# Revit family: FF30_Edge.rfa
name_source: partatom
category: 门
units: mm (PartAtom-declared; Revit-internal decimal feet)

## family parameters
主体 = 墙
共享 = 否
加载时剪切的空心 = 否
总是垂直 = 是
房间计算点 = 否

## types (16) — shared parameters
Height above ground = 4' - 0"
Height of Door = 14' - 0"
Width of Switch = 1' - 0"
depth of Switch = 0' - 5"
height of Switch = 1' - 4"
高度 = 14' - 0"
默认高程 = 0' - 0"

## per-type parameters (varying)
| type | LAYOUT K | LAYOUT L | LAYOUT M | LAYOUT N | LAYOUT P | LAYOUT Q | LAYOUT R | LAYOUT S | Width | Width of Door | 宽度 |
| LAYOUT K 14'x14' | 是 | 否 | 否 | 否 | 否 | 否 | 否 | 否 | 14' - 0" | 14' - 0" | 14' - 0" |
| LAYOUT L 14'x14' | 否 | 是 | 否 | 否 | 否 | 否 | 否 | 否 | 14' - 0" | 14' - 0" | 14' - 0" |
| LAYOUT M 14'x14' | 否 | 否 | 是 | 否 | 否 | 否 | 否 | 否 | 14' - 0" | 14' - 0" | 14' - 0" |
| LAYOUT N 14'x14' | 否 | 否 | 否 | 是 | 否 | 否 | 否 | 否 | 14' - 0" | 14' - 0" | 14' - 0" |
| LAYOUT P 14'x14' | 否 | 否 | 否 | 否 | 是 | 否 | 否 | 否 | 14' - 0" | 14' - 0" | 14' - 0" |
| LAYOUT Q 14'x14' | 否 | 否 | 否 | 否 | 否 | 是 | 否 | 否 | 14' - 0" | 14' - 0" | 14' - 0" |
| LAYOUT K 12'x14' | 是 | 否 | 否 | 否 | 否 | 否 | 否 | 否 | 12' - 0" | 12' - 0" | 12' - 0" |
| LAYOUT L 12'x14' | 否 | 是 | 否 | 否 | 否 | 否 | 否 | 否 | 12' - 0" | 12' - 0" | 12' - 0" |
| LAYOUT M 12'x14' | 否 | 否 | 是 | 否 | 否 | 否 | 否 | 否 | 12' - 0" | 12' - 0" | 12' - 0" |
| LAYOUT N 12'x14' | 否 | 否 | 否 | 是 | 否 | 否 | 否 | 否 | 12' - 0" | 12' - 0" | 12' - 0" |
| LAYOUT P 12'x14' | 否 | 否 | 否 | 否 | 是 | 否 | 否 | 否 | 12' - 0" | 12' - 0" | 12' - 0" |
| LAYOUT Q 12'x14' | 否 | 否 | 否 | 否 | 否 | 是 | 否 | 否 | 12' - 0" | 12' - 0" | 12' - 0" |
| LAYOUT R 12'x14' | 否 | 否 | 否 | 否 | 否 | 否 | 是 | 否 | 12' - 0" | 12' - 0" | 12' - 0" |
| LAYOUT R 14'x14' | 否 | 否 | 否 | 否 | 否 | 否 | 是 | 否 | 14' - 0" | 14' - 0" | 14' - 0" |
| LAYOUT S 12'x14' | 否 | 否 | 否 | 否 | 否 | 否 | 否 | 是 | 12' - 0" | 12' - 0" | 12' - 0" |
| LAYOUT S 14'x14' | 否 | 否 | 否 | 否 | 否 | 否 | 否 | 是 | 14' - 0" | 14' - 0" | 14' - 0" |

## geometry (parser evidence)
native form markers: Sweep x139
no freeform markers — native parametric forms only
